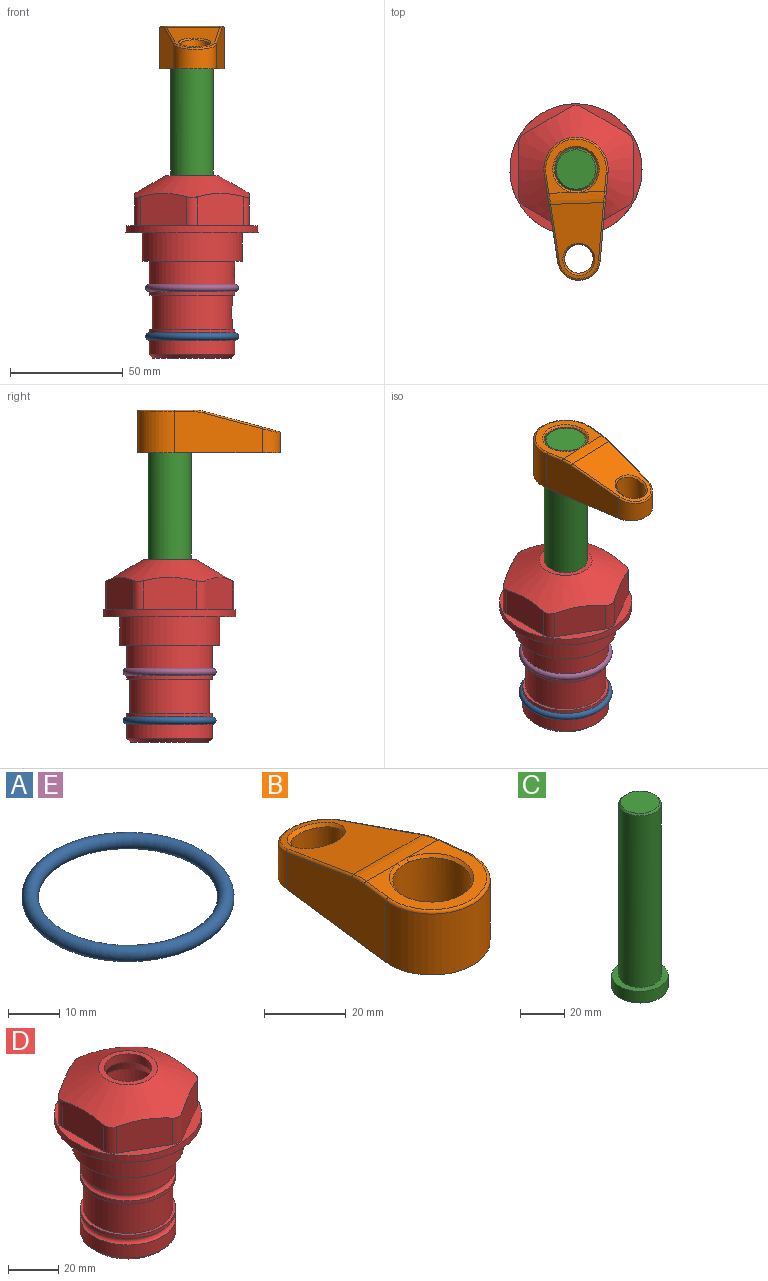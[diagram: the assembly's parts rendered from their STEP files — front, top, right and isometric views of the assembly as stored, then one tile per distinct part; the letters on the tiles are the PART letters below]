
ASSEMBLY  parts=5 mates=4
PART A: 1 faces, bbox 44.7x44.7x3.2 mm
  f0: torus R=19.05mm, axis (0,0,1), area 1193.9mm2
PART B: 31 faces, bbox 31.7x65.5x19.8 mm
  f0: plane 39.12x18.26mm, normal (0.99,0.12,0), area 612.2mm2, adj f1,f4,f7,f11,f13,f15
  f1: cylinder r=9.53mm len=18.91mm, axis (0,0,-1), area 296.1mm2, adj f0,f2,f7,f17
  f2: plane 39.12x18.26mm, normal (-0.99,0.12,0), area 612.2mm2, adj f1,f4,f7,f12,f14,f16
  f3: cylinder r=6.35mm len=12.7mm, axis (0,0,-1), area 362.4mm2, adj f7,f18
  f4: cylinder r=14.29mm len=28.58mm, axis (0,0,-1), area 882.2mm2, adj f0,f2,f7,f10
  f5: cylinder r=9.53mm len=19.05mm, axis (0,0,-1), area 1092.6mm2, adj f7,f19,f20
  f6: plane 26.99x23.69mm, normal (0,0,1), area 216.2mm2, adj f9,f10,f11,f12,f19
  f7: plane 63.5x28.58mm, normal (0,0,-1), area 661.8mm2, adj f0,f1,f2,f3,f4,f5,f22,f23
  f8: plane 33.52x23.6mm, normal (0,0.26,0.97), area 486mm2, adj f9,f15,f16,f17,f18
  f9: cylinder r=19.05mm len=24.72mm, axis (1,0,0), area 120.4mm2, adj f6,f8,f13,f14,f20
  f10: torus R=13.49mm, axis (0,0,1), area 59mm2, adj f4,f6,f11,f12
  f11: cylinder r=0.79mm len=8.67mm, axis (0.12,-0.99,0), area 10.8mm2, adj f0,f6,f10,f13
  f12: cylinder r=0.79mm len=8.67mm, axis (0.12,0.99,0), area 10.8mm2, adj f2,f6,f10,f14
  f13: bspline ~4.95x1.42mm, area 6.1mm2, adj f0,f9,f11,f15
  f14: bspline ~4.95x1.42mm, area 6.1mm2, adj f2,f9,f12,f16
  f15: cylinder r=0.79mm len=25.95mm, axis (0.12,-0.96,0.26), area 32.9mm2, adj f0,f8,f13,f17
  f16: cylinder r=0.79mm len=25.95mm, axis (0.12,0.96,-0.26), area 32.9mm2, adj f2,f8,f14,f17
  f17: bspline ~18.91x8.38mm, area 30mm2, adj f1,f8,f15,f16
  f18: bspline ~14.29x14.29mm, area 48.3mm2, adj f3,f8
  f19: cone r=9.53mm half-angle=45deg, axis (0,0,1), area 66.5mm2, adj f5,f6,f20
  f20: bspline ~3.22x0.96mm, area 3.5mm2, adj f5,f9,f19
  f21: plane 2.75x2.72mm, normal (0,0,-1), area 2.9mm2, adj f23,f25,f28
  f22: plane 23.05x15.88mm, normal (-0.99,-0.12,0), area 323.6mm2, adj f7,f25,f26,f27,f28,f29
  f23: plane 23.05x15.88mm, normal (0.99,-0.12,0), area 323.6mm2, adj f7,f21,f25,f27,f28,f30
  f24: cylinder r=9.53mm len=10.69mm, axis (0,0,-1), area 114.7mm2, adj f7,f27,f29,f30
  f25: cylinder r=12.7mm len=20.59mm, axis (0,0,-1), area 381.1mm2, adj f7,f21,f22,f23,f26,f28
  f26: plane 2.75x2.72mm, normal (0,0,-1), area 2.9mm2, adj f22,f25,f28
  f27: plane 19.72x18.37mm, normal (0,-0.26,-0.97), area 291.8mm2, adj f22,f23,f24,f28,f29,f30
  f28: cylinder r=15.88mm len=19.92mm, axis (1,0,0), area 54.8mm2, adj f21,f22,f23,f25,f26,f27
  f29: cylinder r=1.59mm len=11mm, axis (0,0,-1), area 34.7mm2, adj f7,f22,f24,f27
  f30: cylinder r=1.59mm len=11mm, axis (0,0,-1), area 34.7mm2, adj f7,f23,f24,f27
PART C: 6 faces, bbox 25.4x25.4x101.6 mm
  f0: plane 17.46x17.46mm, normal (0,0,1), area 239.5mm2, adj f5
  f1: plane 25.4x25.4mm, normal (0,0,-1), area 506.7mm2, adj f2
  f2: cylinder r=12.7mm len=25.4mm, axis (0,0,1), area 506.7mm2, adj f1,f3
  f3: plane 25.4x25.4mm, normal (0,0,1), area 221.7mm2, adj f2,f4
  f4: cylinder r=9.53mm len=94.46mm, axis (0,0,1), area 5653mm2, adj f3,f5
  f5: cone r=8.73mm half-angle=45deg, axis (0,0,-1), area 64.4mm2, adj f0,f4
PART D: 36 faces, bbox 58.7x58.7x81 mm
  f0: cylinder r=17.78mm len=35.56mm, axis (0,0,1), area 1670.8mm2, adj f23,f24,f31
  f1: cylinder r=19.05mm len=38.1mm, axis (0,0,1), area 1191.9mm2, adj f26,f27,f30
  f2: plane 58.66x58.66mm, normal (0,0,-1), area 1150.6mm2, adj f3,f28
  f3: cylinder r=29.33mm len=58.66mm, axis (0,0,-1), area 585.1mm2, adj f2,f4
  f4: plane 58.66x58.66mm, normal (0,0,1), area 475.9mm2, adj f3,f5,f6,f7,f8,f9,f10,f11
  f5: plane 20.32x14.34mm, normal (-0.5,0.87,0), area 324.4mm2, adj f4,f15,f16,f17
  f6: plane 20.32x14.34mm, normal (0.5,0.87,0), area 324.4mm2, adj f4,f14,f15,f17
  f7: plane 23.48x14.34mm, normal (1,0,0), area 324.4mm2, adj f4,f13,f14,f17
  f8: plane 20.32x14.34mm, normal (0.5,-0.87,0), area 324.4mm2, adj f4,f12,f13,f17
  f9: plane 20.32x14.34mm, normal (-0.5,-0.87,0), area 324.4mm2, adj f4,f11,f12,f17
  f10: plane 23.48x14.34mm, normal (-1,0,0), area 324.4mm2, adj f4,f11,f16,f17
  f11: cylinder r=5.08mm len=12.85mm, axis (0,0,-1), area 67.2mm2, adj f4,f9,f10,f17
  f12: cylinder r=5.08mm len=12.85mm, axis (0,0,-1), area 67.2mm2, adj f4,f8,f9,f17
  f13: cylinder r=5.08mm len=12.85mm, axis (0,0,-1), area 67.2mm2, adj f4,f7,f8,f17
  f14: cylinder r=5.08mm len=12.85mm, axis (0,0,-1), area 67.2mm2, adj f4,f6,f7,f17
  f15: cylinder r=5.08mm len=12.85mm, axis (0,0,-1), area 67.2mm2, adj f4,f5,f6,f17
  f16: cylinder r=5.08mm len=12.85mm, axis (0,0,-1), area 67.2mm2, adj f4,f5,f10,f17
  f17: cone r=11.73mm half-angle=60deg, axis (0,0,-1), area 2071.8mm2, adj f5,f6,f7,f8,f9,f10,f11,f12
  f18: plane 23.46x23.46mm, normal (0,0,1), area 147.4mm2, adj f17,f35
  f19: plane 34.93x34.93mm, normal (0,0,-1), area 958mm2, adj f29
  f20: cylinder r=19.05mm len=38.1mm, axis (0,0,1), area 760.1mm2, adj f21,f29
  f21: torus R=19.05mm, axis (0,0,1), area 565.3mm2, adj f20,f22
  f22: cylinder r=19.05mm len=38.1mm, axis (0,0,1), area 190mm2, adj f21,f23
  f23: plane 38.1x38.1mm, normal (0,0,1), area 146.9mm2, adj f0,f22
  f24: plane 38.1x38.1mm, normal (0,0,-1), area 146.9mm2, adj f0,f25
  f25: cylinder r=19.05mm len=38.1mm, axis (0,0,1), area 190mm2, adj f24,f26
  f26: torus R=19.05mm, axis (0,0,1), area 565.3mm2, adj f1,f25
  f27: plane 44.45x44.45mm, normal (0,0,-1), area 411.7mm2, adj f1,f28
  f28: cylinder r=22.23mm len=44.45mm, axis (0,0,1), area 1773.5mm2, adj f2,f27
  f29: cone r=19.05mm half-angle=45deg, axis (0,0,1), area 257.5mm2, adj f19,f20
  f30: cylinder r=3.17mm len=6.75mm, axis (-1,0,0), area 128mm2, adj f1,f33
  f31: cylinder r=3.17mm len=6.35mm, axis (-1,0,0), area 102.5mm2, adj f0,f33
  f32: plane 25.4x25.4mm, normal (0,0,1), area 506.7mm2, adj f33
  f33: cylinder r=12.7mm len=66.42mm, axis (0,0,-1), area 5236.2mm2, adj f30,f31,f32,f34
  f34: cone r=9.53mm half-angle=30deg, axis (0,0,-1), area 443.4mm2, adj f33,f35
  f35: cylinder r=9.53mm len=19.05mm, axis (0,0,-1), area 240.9mm2, adj f18,f34
PART E: same geometry as A
PLACE A t=(0,0,-21.59)mm
PLACE B rot(axis=(0,0,-1),178.1deg) t=(0,0,28.35)mm
PLACE C rot(axis=(0,0,-1),178.1deg) t=(0,0,27.55)mm
PLACE D at identity fixed
PLACE E at identity
MATE fastened B.f4 <-> C.f2  axis (0,0,1) through (0,0,91.05)mm
MATE fastened D.f0 <-> A.f0  axis (0,0,1) through (0,0,-46.1)mm
MATE fastened D.f0 <-> E.f0  axis (0,0,1) through (0,0,-24.51)mm
MATE cylindrical C.f2 <-> D.f0  axis (0,0,-1) through (0,0,-10.55)mm
